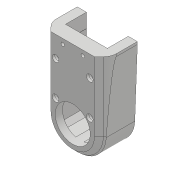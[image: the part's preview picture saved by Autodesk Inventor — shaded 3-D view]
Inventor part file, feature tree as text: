
AUTODESK INVENTOR PART (.ipt)
format: ipt  version: 2018 (Build 220112000, 112)  size: 726,016 bytes
history: native  units: mm
features: sketch x34, projected_geometry x31, extrude x27, hole x9, fillet x7, chamfer x3, mirror x1
ambient origin geometry x8: Origin, YZ Plane, XZ Plane, XY Plane, X Axis, Y Axis, Z Axis, Center Point
bodies: Solid1 (feature_tree)
feature tree (112):
  extrude  "Extrusion1"  Depth=45.0mm
  extrude  "Extrusion2"  Depth=2.25mm
  hole  "Hole1"  [1 undecoded]
  hole  "Hole2"  [1 undecoded]
  fillet  "Fillet1"  Radius=14.0mm
  extrude  "Extrusion3"  Depth=18.5mm
  extrude  "Extrusion4"  Depth=10.0mm
  extrude  "Extrusion5"  Depth=2.0mm
  extrude  "Extrusion6"  Depth=2.0mm
  hole  "Hole3"  [1 undecoded]
  extrude  "Extrusion7"  Depth=0.5mm
  extrude  "Extrusion8"  Depth=5.0mm TaperAngle=0.0deg
  extrude  "Extrusion9"  Depth=10.0mm
  extrude  "Extrusion10"  Depth=10.0mm
  extrude  "Extrusion11"  Depth=14.5mm
  extrude  "Extrusion12"  Depth=14.5mm
  extrude  "Extrusion13"  Depth=5.0mm
  extrude  "Extrusion14"  Depth=5.0mm
  extrude  "Extrusion15"  Depth=5.0mm
  extrude  "Extrusion16"  Depth=5.0mm
  extrude  "Extrusion17"  Depth=1.0mm
  chamfer  "Chamfer1"  Distance=1.0mm
  fillet  "Fillet7"  Radius=20.7mm
  fillet  "Fillet8"  Radius=32.0mm
  mirror  "Mirror1"
  extrude  "Extrusion19"  Depth=1.0mm TaperAngle=0.0deg
  extrude  "Extrusion20"  Depth=8.0mm
  extrude  "Extrusion21"  Depth=0.2mm TaperAngle=0.0deg
  extrude  "Extrusion22"  Depth=0.5mm TaperAngle=0.0deg
  extrude  "Extrusion23"  Depth=5.0mm TaperAngle=0.0deg
  chamfer  "Chamfer2"  Distance=5.0mm
  fillet  "Fillet9"  Radius=0.2mm
  extrude  "Extrusion24"  Depth=2.0mm TaperAngle=45.0deg
  extrude  "Extrusion27"  Depth=0.5mm
  extrude  "Extrusion28"  Depth=1.8mm TaperAngle=0.0deg
  hole  "Hole6"  [1 undecoded]
  sketch  "Sketch39"  dims[d105=1.5mm d114=0.5mm]
  hole  "Hole7"  [1 undecoded]
  hole  "Hole8"  [1 undecoded]
  fillet  "Fillet10"  Radius=5.0mm
  hole  "Hole9"  [1 undecoded]
  extrude  "Extrusion29"  Depth=20.75mm
  chamfer  "Chamfer4"  Distance=10.0mm
  hole  "Hole10"  [1 undecoded]
  fillet  "Fillet11"  Radius=18.0mm
  hole  "Hole11"  [1 undecoded]
  fillet  "Fillet12"  Radius=0.05mm
  extrude  "Extrusion30"  Depth=7.0mm TaperAngle=0.0deg
  sketch  "Sketch1"  dims[d0=24.5mm d1=45.0mm]
  sketch  "Sketch2"  dims[d2=1.95mm d3=0.0mm d4=2.25mm]
  projected_geometry  "Projected Loop1"
  sketch  "Sketch3"  dims[d5=20.0mm d6=2.25mm]
  projected_geometry  "Projected Loop2"
  sketch  "Sketch4"  dims[d7=5.25mm d8=5.25mm d9=14.0mm]
  projected_geometry  "Projected Loop3"
  sketch  "Sketch5"  dims[d10=5.25mm d11=18.5mm]
  projected_geometry  "Projected Loop4"
  sketch  "Sketch6"  dims[d12=10.0mm d13=0.0mm d14=20.5mm]
  projected_geometry  "Projected Loop5"
  sketch  "Sketch7"  dims[d15=2.0mm d16=2.195mm]
  projected_geometry  "Projected Loop6"
  sketch  "Sketch8"  dims[d17=2.0mm]
  projected_geometry  "Projected Loop7"
  sketch  "Sketch9"  dims[d18=2.4mm d19=6.0mm d20=4.4mm d21=2.0mm d22=90.0deg d23=8.0mm d24=20.594885mm d25=20.5mm]
  projected_geometry  "Projected Loop8"
  projected_geometry  "Projected Loop9"
  sketch  "Sketch10"  dims[d26=26.65mm d27=2.0mm]
  projected_geometry  "Projected Loop10"
  projected_geometry  "Projected Loop11"
  sketch  "Sketch11"  dims[d28=2.0mm]
  projected_geometry  "Projected Loop12"
  sketch  "Sketch12"  dims[d29=2.4mm d30=6.0mm d31=4.4mm d32=2.0mm d33=90.0deg d34=8.0mm d35=20.594885mm d36=0.5mm]
  sketch  "Sketch13"  dims[d37=18.0mm d38=5.0mm d39=0.0mm]
  sketch  "Sketch14"  dims[d41=10.0mm d42=0.0mm d43=24.5mm]
  projected_geometry  "Projected Loop13"
  sketch  "Sketch15"  dims[d44=1.15mm d45=0.0mm d46=10.0mm]
  sketch  "Sketch16"  dims[d47=21.0mm d48=14.5mm]
  projected_geometry  "Projected Loop14"
  sketch  "Sketch17"  dims[d49=20.0mm d50=14.5mm]
  projected_geometry  "Projected Loop15"
  sketch  "Sketch18"  dims[d51=24.5mm d52=5.0mm]
  projected_geometry  "Projected Loop16"
  sketch  "Sketch19"  dims[d53=5.0mm d54=2.25mm]
  projected_geometry  "Projected Loop17"
  sketch  "Sketch20"  dims[d55=2.25mm d56=5.0mm]
  projected_geometry  "Projected Loop18"
  sketch  "Sketch25"  dims[d57=5.0mm d58=9.0mm]
  projected_geometry  "Projected Loop22"
  sketch  "Sketch26"  dims[d59=14.75mm d60=4.0mm d61=1.0mm d62=0.0mm d63=20.7mm]
  projected_geometry  "Projected Loop23"
  sketch  "Sketch27"  dims[d64=2.4mm d65=6.0mm d66=4.4mm d67=2.0mm d68=90.0deg d69=8.0mm d70=20.594885mm d72=32.0mm]
  projected_geometry  "Projected Loop25"
  sketch  "Sketch29"  dims[d73=5.0mm d74=0.0mm d75=1.0mm d76=0.0mm]
  projected_geometry  "Projected Loop26"
  sketch  "Sketch30"  dims[d77=12.25mm d78=0.0mm d80=8.0mm]
  projected_geometry  "Projected Loop27"
  sketch  "Sketch32"  dims[d81=4.5mm d82=0.0mm d84=0.2mm d85=0.0mm]
  projected_geometry  "Projected Loop28"
  projected_geometry  "Projected Loop29"
  sketch  "Sketch36"  dims[d86=21.0mm d87=0.5mm d88=0.0mm]
  projected_geometry  "Projected Loop33"
  sketch  "Sketch37"  dims[d91=8.0mm d92=0.0mm d93=5.0mm d94=0.0mm d95=5.0mm d96=0.0mm d98=0.2mm d99=0.0mm]
  projected_geometry  "Projected Loop34"
  sketch  "Sketch38"  dims[d100=0.2mm d101=0.0mm d102=2.5mm d103=2.0mm d104=45.0deg]
  projected_geometry  "Projected Loop35"
  sketch  "Sketch41"  dims[d128=1.8mm d129=0.0mm d130=1.8mm d131=0.0mm]
  projected_geometry  "Projected Loop36"
  sketch  "Sketch42"  dims[d133=36.055mm d134=4.2225mm]
  projected_geometry  "Projected Loop37"
  sketch  "Sketch43"  dims[d135=4.2225mm d136=2.0mm d137=0.0mm]
  projected_geometry  "Projected Loop38"
  sketch  "Sketch44"  dims[d138=2.0mm d139=0.0mm d140=2.0mm d141=0.0mm d142=5.0mm d143=2.0mm d144=45.0deg d145=8.0mm d147=33.0mm d148=10.0mm d149=0.0mm d161=20.75mm d162=18.0mm d163=25.0mm d164=0.05mm d165=7.0mm d166=0.0mm d167=1.5mm d168=0.0mm d169=3.0mm d170=12.0mm d171=2.1mm d172=6.0mm d173=6.3mm d174=2.0mm d175=90.0deg d176=8.0mm d177=20.594885mm d178=1.567mm d179=36.0mm d180=4.4mm d181=2.0mm d182=90.0deg d183=36.0mm d184=20.594885mm d185=4.0mm d186=5.029mm d187=4.4mm d188=2.0mm d189=90.0deg d190=15.0mm d191=0.0mm d192=0.5mm d193=2.1mm d194=5.029mm d195=4.4mm d196=2.0mm d197=90.0deg d198=20.75mm d199=0.0mm d200=15.0mm d201=1.5mm d202=0.0mm d203=1.5mm d204=2.0mm d205=45.0deg d206=4.0mm d207=5.029mm d208=4.4mm d209=2.0mm d210=90.0deg d211=2.2mm d212=0.0mm d213=0.75mm d214=4.0mm d215=5.029mm d216=4.4mm d217=2.0mm d218=90.0deg d219=2.2mm d220=0.0mm d221=0.75mm d222=20.75mm d223=0.0mm]
note: 9 required parameter values undecoded (feature->parameter linkage not recoverable at this tier; creation-order binding heuristic only, values carry confidence <= 0.55)
